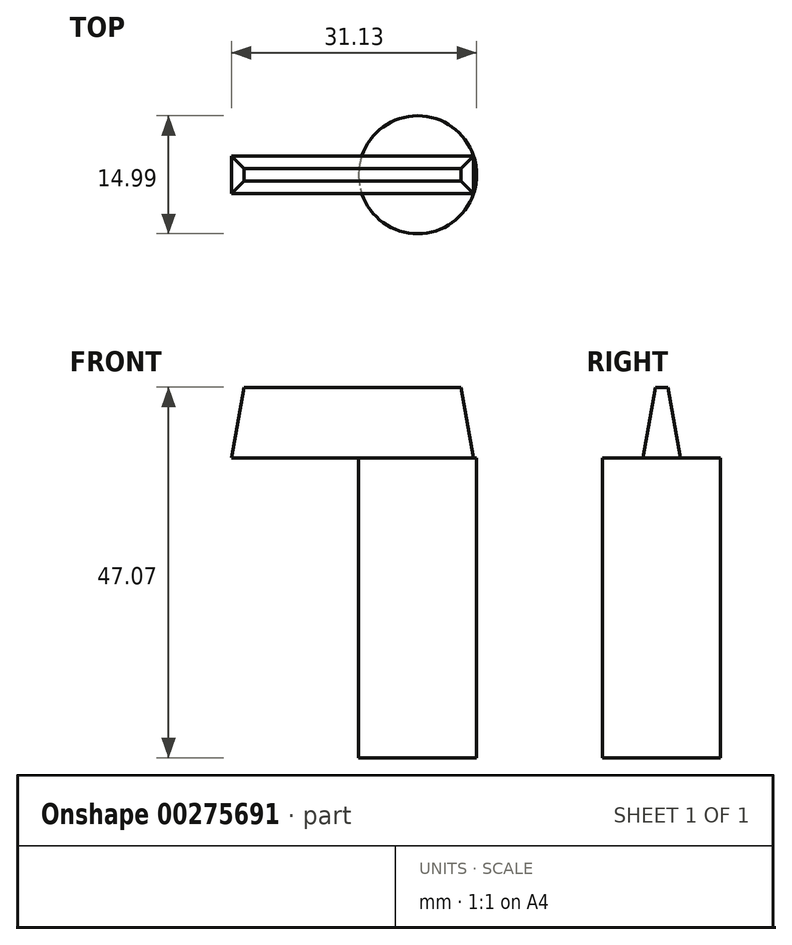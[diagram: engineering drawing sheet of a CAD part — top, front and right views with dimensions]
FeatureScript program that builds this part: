
annotation { "Feature Type Name" : "Feature", "Feature Type Description" : "" }
export const myFeature = defineFeature(function(context is Context, id is Id, definition is map)
    precondition{}
    {
        {
            var Q0;
            Q0=qCreatedBy(makeId("Top.planeOp"),FACE);
            var sketch = newSketch(context, id + "F0", { "sketchPlane" : qUnion([Q0])});
            skCircle(sketch, "E0", {"center": v(23.64, 23.26) * mm, "radius": 7.5 * mm});
            skSolve(sketch);
        }
        {
            var Q0;
            Q0=makeQuery(id+"F0.imprint","IMPRINT",FACE,{"disambiguationData":[TD([[makeQuery(id+"F0.imprint","IMPRINT",EDGE,{"derivedFrom":sQuery(id+"F0.wireOp",EDGE,"E0")}),1.0]])]});
            extrude(context, id + "F1", {"entities" : qUnion([Q0]), "depth" : 38.1 * mm});
        }
        {
            var Q0;
            Q0=makeQuery(id+"F1.opExtrude","CAP_FACE",FACE,{"disambiguationData":[OSD([sQuery(id+"F0.wireOp",EDGE,"E0")])],"isStart":false});
            var sketch = newSketch(context, id + "F2", { "sketchPlane" : qUnion([Q0])});
            skLineSegment(sketch, "E1.bottom", {"start": v(0, 20.88) * mm, "end": v(30.74, 20.88) * mm});
            skLineSegment(sketch, "E1.top", {"start": v(0, 25.64) * mm, "end": v(30.74, 25.64) * mm});
            skLineSegment(sketch, "E1.left", {"start": v(0, 20.88) * mm, "end": v(0, 25.64) * mm});
            skLineSegment(sketch, "E1.right", {"start": v(30.74, 20.88) * mm, "end": v(30.74, 25.64) * mm});
            skSolve(sketch);
        }
        {
            var Q0;
            {var subQ0=sQuery(id+"F2.wireOp",EDGE,"E1.right");Q0=makeQuery(id+"F2.imprint","IMPRINT",FACE,{"disambiguationData":[TD([[makeQuery(id+"F2.imprint","IMPRINT",EDGE,{"derivedFrom":subQ0}),1.0]])]});}
            var Q1;
            {var subQ0=sQuery(id+"F2.wireOp",EDGE,"E1.left");Q1=makeQuery(id+"F2.imprint","IMPRINT",FACE,{"disambiguationData":[TD([[makeQuery(id+"F2.imprint","IMPRINT",EDGE,{"derivedFrom":subQ0}),-1.0]])]});}
            extrude(context, id + "F3", {"entities" : qUnion([Q0, Q1]), "operationType" : NewBodyOperationType.ADD, "depth" : 8.97 * mm, "hasDraft" : true, "draftAngle" : 10 * degree, "draftPullDirection" : true});
        }
    });
